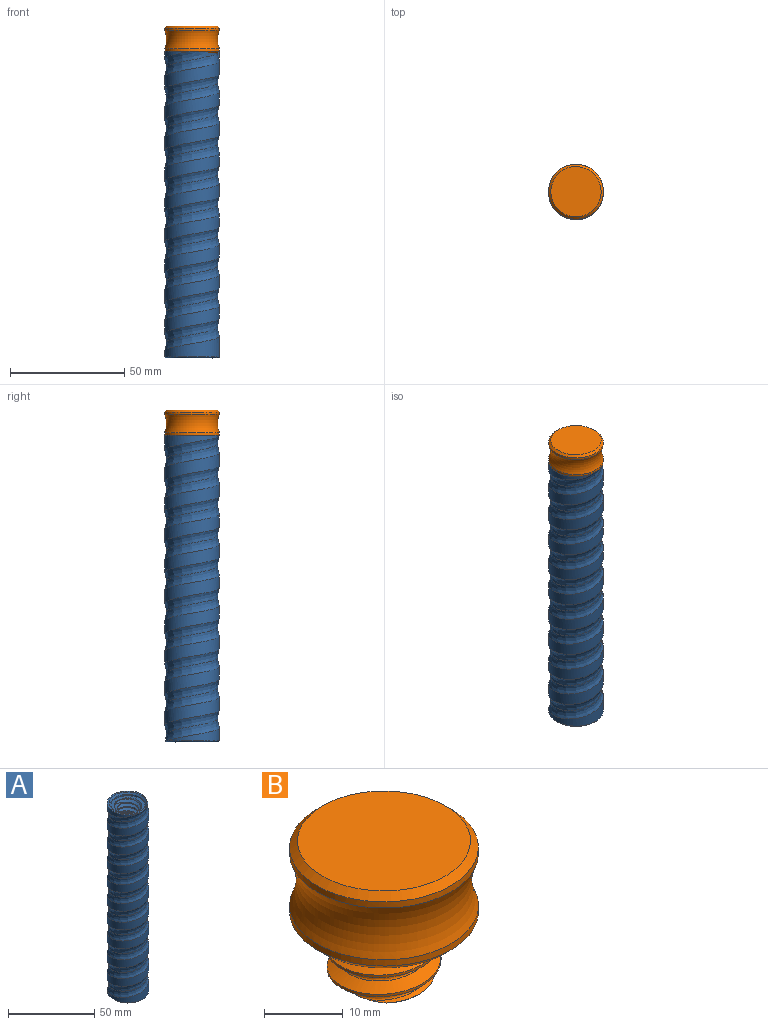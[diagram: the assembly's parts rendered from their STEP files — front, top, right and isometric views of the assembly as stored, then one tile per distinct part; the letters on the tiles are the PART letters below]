
ASSEMBLY  parts=2 mates=1
PART A: 20 faces, bbox 28.1x28.1x147.4 mm
  f0: plane 23.06x23.06mm, normal (0,0,-1), area 413.5mm2, adj f1,f15,f19
  f1: cone r=12mm half-angle=45deg, axis (0,0,1), area 39.8mm2, adj f0,f5,f15,f19
  f2: plane 20x20mm, normal (0,0,1), area 113.1mm2, adj f3,f6
  f3: cylinder r=10mm len=20mm, axis (0,0,1), area 62.8mm2, adj f2,f17
  f4: plane 24.31x24.23mm, normal (0,0,1), area 62.7mm2, adj f5,f16,f17,f18
  f5: cylinder r=12mm len=133.5mm, axis (0,0,1), area 3858.5mm2, adj f1,f4,f15,f16,f18,f19
  f6: cone r=11mm half-angle=45deg, axis (0,0,1), area 66.8mm2, adj f2,f11,f12,f13,f14
  f7: plane 15x15mm, normal (0,0,1), area 176.7mm2, adj f8
  f8: cylinder r=7.5mm len=120mm, axis (0,0,1), area 5654.9mm2, adj f7,f9,f10
  f9: plane 10.97x4.75mm, normal (0,0,1), area 4mm2, adj f8,f11,f13,f14
  f10: plane 15.56x14.33mm, normal (0,0,-1), area 26.9mm2, adj f8,f12,f13,f14
  f11: bspline ~18.5x16.02mm, area 71.5mm2, adj f6,f9,f13,f14
  f12: cylinder r=6.25mm len=12.5mm, axis (0,0,-1), area 81.3mm2, adj f6,f10,f13,f14
  f13: bspline ~18.18x15.75mm, area 251.6mm2, adj f6,f9,f10,f11,f12
  f14: bspline ~18.18x15.75mm, area 252.5mm2, adj f6,f9,f10,f11,f12
  f15: bspline ~140.18x27.51mm, area 2836.1mm2, adj f0,f1,f5,f16,f18,f19
  f16: bspline ~140.18x27.51mm, area 2851.6mm2, adj f4,f5,f15,f18,f19
  f17: cone r=10mm half-angle=45deg, axis (0,0,1), area 93.3mm2, adj f3,f4
  f18: bspline ~6.04x2.22mm, area 6.2mm2, adj f4,f5,f15,f16
  f19: bspline ~5.36x2.22mm, area 5.4mm2, adj f0,f1,f5,f15,f16
PART B: 13 faces, bbox 31.2x31.2x24.1 mm
  f0: plane 12.08x11.59mm, normal (0,0,-1), area 107.7mm2, adj f5,f6,f7,f8
  f1: cylinder r=7.25mm len=14.5mm, axis (0,0,1), area 43.8mm2, adj f3,f6,f7,f8
  f2: cylinder r=12mm len=24mm, axis (0,0,1), area 72.8mm2, adj f4,f9
  f3: plane 22.82x22.82mm, normal (0,0,-1), area 253.8mm2, adj f1,f4,f5,f6,f7
  f4: cone r=12mm half-angle=45deg, axis (0,0,1), area 102.2mm2, adj f2,f3
  f5: bspline ~12.99x11.25mm, area 87.5mm2, adj f0,f3,f6,f7
  f6: bspline ~16.74x14.5mm, area 215.4mm2, adj f0,f1,f3,f5,f8
  f7: bspline ~16.74x14.5mm, area 214.9mm2, adj f0,f1,f3,f5,f8
  f8: cone r=8mm half-angle=45deg, axis (0,0,1), area 26.5mm2, adj f0,f1,f6,f7
  f9: torus R=21.15mm, axis (0,0,1), area 596.8mm2, adj f2,f12
  f10: plane 22x22mm, normal (0,0,1), area 380.1mm2, adj f11
  f11: cone r=11mm half-angle=45deg, axis (0,0,-1), area 102.2mm2, adj f10,f12
  f12: cylinder r=12mm len=24mm, axis (0,0,1), area 72.8mm2, adj f9,f11
PLACE A t=(-37.96,-14.14,-101.66)mm
PLACE B t=(-37.96,-14.14,22.48)mm
MATE slider B.f1 <-> A.f1  axis (0,0,1) through (-37.96,-14.14,27.61)mm
